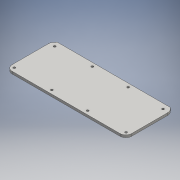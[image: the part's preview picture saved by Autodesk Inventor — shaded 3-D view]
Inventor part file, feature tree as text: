
AUTODESK INVENTOR PART (.ipt)
format: ipt  version: 2016 (Build 200138000, 138)  size: 112,640 bytes
history: native  units: mm
features: extrude x1, sketch x1
ambient origin geometry x8: Origin, YZ Plane, XZ Plane, XY Plane, X Axis, Y Axis, Z Axis, Center Point
bodies: Solid1 (feature_tree)
feature tree (2):
  extrude  "Extrusion1"  [1 undecoded]
  sketch  "Sketch1"  dims[d0=5.0mm d1=0.0mm]
note: 1 required parameter value undecoded (feature->parameter linkage not recoverable at this tier; creation-order binding heuristic only, values carry confidence <= 0.55)
